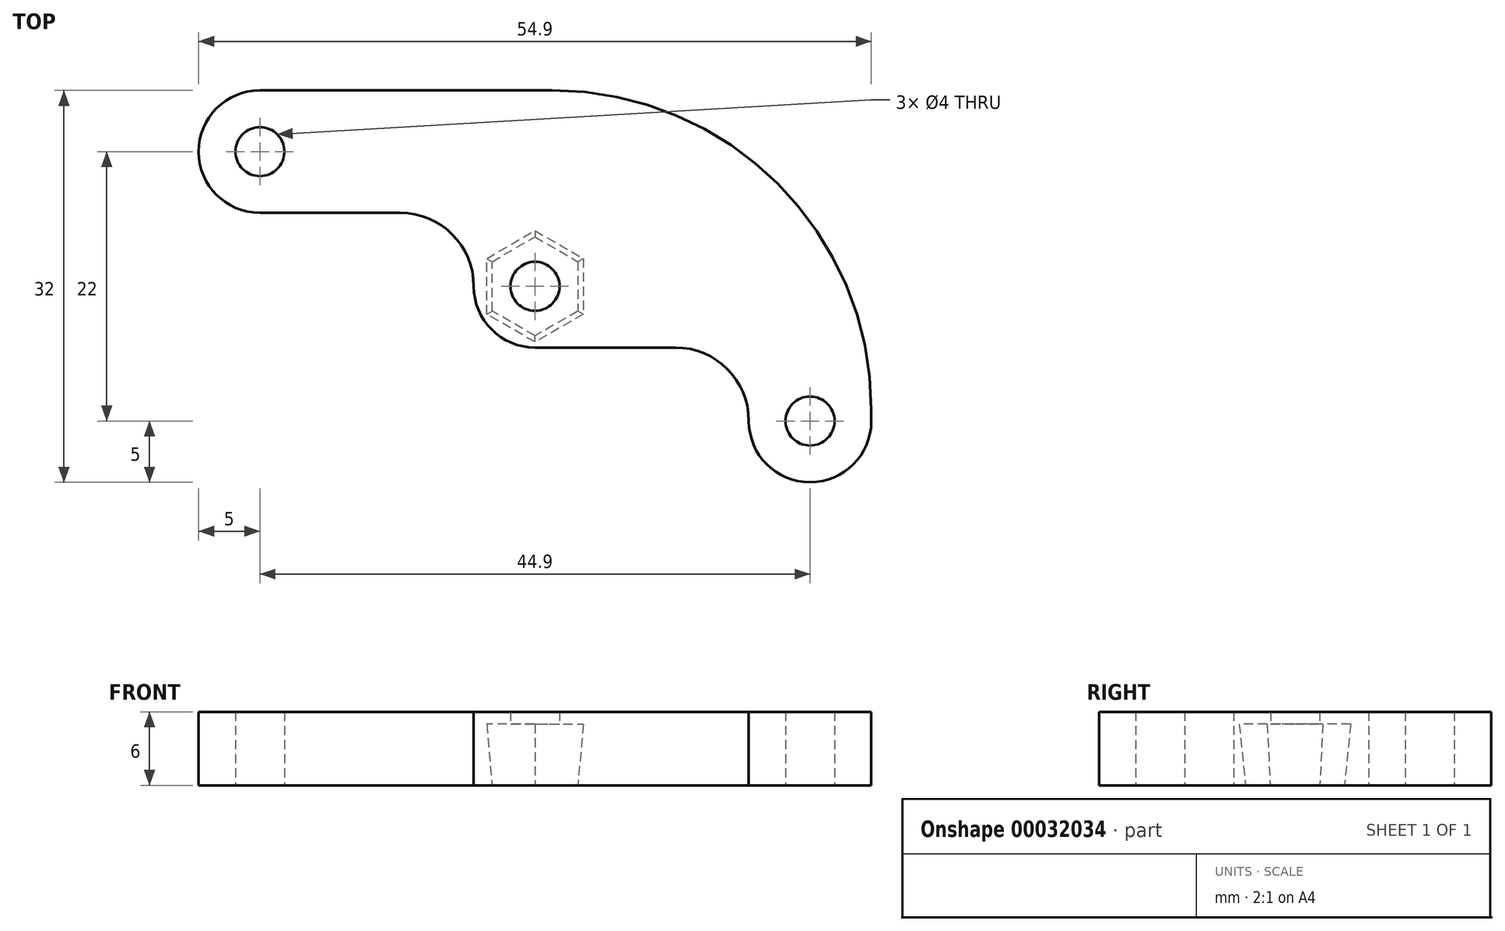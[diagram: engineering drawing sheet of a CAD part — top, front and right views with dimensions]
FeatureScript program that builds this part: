
annotation { "Feature Type Name" : "Feature", "Feature Type Description" : "" }
export const myFeature = defineFeature(function(context is Context, id is Id, definition is map)
    precondition{}
    {
        {
            var Q0;
            Q0=qCreatedBy(makeId("Top.planeOp"),FACE);
            var sketch = newSketch(context, id + "F0", { "sketchPlane" : qUnion([Q0])});
            skCircle(sketch, "E0", {"center": v(0, 0) * mm, "radius": 2 * mm});
            skCircle(sketch, "E1", {"center": v(22.45, -11) * mm, "radius": 2 * mm});
            skCircle(sketch, "E2", {"center": v(-22.45, 11) * mm, "radius": 2 * mm});
            skLineSegment(sketch, "E3", {"start": v(0, 16) * mm, "end": v(0, 6) * mm, "construction": true});
            skLineSegment(sketch, "E4", {"start": v(0, 6) * mm, "end": v(0, -6) * mm, "construction": true});
            skLineSegment(sketch, "E5", {"start": v(0, -6) * mm, "end": v(0, -16) * mm, "construction": true});
            skLineSegment(sketch, "E6", {"start": v(0, 11) * mm, "end": v(-22.45, 11) * mm, "construction": true});
            skLineSegment(sketch, "E7", {"start": v(0, -11) * mm, "end": v(22.45, -11) * mm, "construction": true});
            skCircle(sketch, "E8", {"center": v(-22.45, 11) * mm, "radius": 5 * mm, "construction": true});
            skCircle(sketch, "E9", {"center": v(0, 0) * mm, "radius": 5 * mm, "construction": true});
            skCircle(sketch, "E10", {"center": v(22.45, -11) * mm, "radius": 5 * mm, "construction": true});
            skLineSegment(sketch, "E11", {"start": v(-22.45, 6) * mm, "end": v(-11, 6) * mm});
            skLineSegment(sketch, "E12", {"start": v(-22.45, 16) * mm, "end": v(1.4, 16) * mm});
            skArc(sketch, "E13", {"start": v(-5, 0) * mm, "mid": v(-6.76, 4.24) * mm, "end": v(-11, 6) * mm});
            skArc(sketch, "E14", {"start": v(17.45, -11) * mm, "mid": v(22.45, -16) * mm, "end": v(27.45, -11) * mm});
            skArc(sketch, "E15", {"start": v(-22.45, 16) * mm, "mid": v(-27.45, 11) * mm, "end": v(-22.45, 6) * mm});
            skArc(sketch, "E16", {"start": v(-5, 0) * mm, "mid": v(-3.54, -3.54) * mm, "end": v(0, -5) * mm});
            skLineSegment(sketch, "E17", {"start": v(0, -5) * mm, "end": v(11.45, -5) * mm});
            skArc(sketch, "E18", {"start": v(17.45, -11) * mm, "mid": v(15.7, -6.76) * mm, "end": v(11.45, -5) * mm});
            skLineSegment(sketch, "E19", {"start": v(0, 5) * mm, "end": v(0, 5) * mm});
            skArc(sketch, "E20", {"start": v(27.45, -10.05) * mm, "mid": v(19.82, 8.37) * mm, "end": v(1.4, 16) * mm});
            skLineSegment(sketch, "E21", {"start": v(27.45, -11) * mm, "end": v(27.45, -10.05) * mm});
            skSolve(sketch);
        }
        {
            var Q0;
            Q0 = qSketchRegion(id + "F0", true);
            extrude(context, id + "F1", {"entities" : qUnion([Q0]), "depth" : 6 * mm});
        }
        {
            var Q0;
            Q0=makeQuery(id+"F1.opExtrude","CAP_FACE",FACE,{"disambiguationData":[OSD([sQuery(id+"F0.wireOp",EDGE,"E0"),sQuery(id+"F0.wireOp",EDGE,"E1"),sQuery(id+"F0.wireOp",EDGE,"E2"),sQuery(id+"F0.wireOp",EDGE,"E11"),sQuery(id+"F0.wireOp",EDGE,"E12"),sQuery(id+"F0.wireOp",EDGE,"E13"),sQuery(id+"F0.wireOp",EDGE,"E14"),sQuery(id+"F0.wireOp",EDGE,"E15"),sQuery(id+"F0.wireOp",EDGE,"E16"),sQuery(id+"F0.wireOp",EDGE,"E17"),sQuery(id+"F0.wireOp",EDGE,"E18"),sQuery(id+"F0.wireOp",EDGE,"E20"),sQuery(id+"F0.wireOp",EDGE,"E21")])],"isStart":true});
            var sketch = newSketch(context, id + "F2", { "sketchPlane" : qUnion([Q0])});
            skCircle(sketch, "E22.cCircle", {"center": v(0, 0) * mm, "radius": 3.5 * mm, "construction": true});
            skLineSegment(sketch, "E22.0", {"start": v(3.5, -2.02) * mm, "end": v(0, -4.04) * mm});
            skLineSegment(sketch, "E22.1", {"start": v(0, -4.04) * mm, "end": v(-3.5, -2.02) * mm});
            skLineSegment(sketch, "E22.2", {"start": v(-3.5, -2.02) * mm, "end": v(-3.5, 2.02) * mm});
            skLineSegment(sketch, "E22.3", {"start": v(-3.5, 2.02) * mm, "end": v(0, 4.04) * mm});
            skLineSegment(sketch, "E22.4", {"start": v(0, 4.04) * mm, "end": v(3.5, 2.02) * mm});
            skLineSegment(sketch, "E22.5", {"start": v(3.5, 2.02) * mm, "end": v(3.5, -2.02) * mm});
            skPoint(sketch, "E22.0.midPoint", {"position": v(1.75, -3.03) * mm});
            skSolve(sketch);
        }
        {
            var Q0;
            Q0 = qSketchRegion(id + "F2", true);
            extrude(context, id + "F3", {"entities" : qUnion([Q0]), "operationType" : NewBodyOperationType.REMOVE, "oppositeDirection" : true, "depth" : 5 * mm, "hasDraft" : true, "draftAngle" : 5 * degree});
        }
    });
